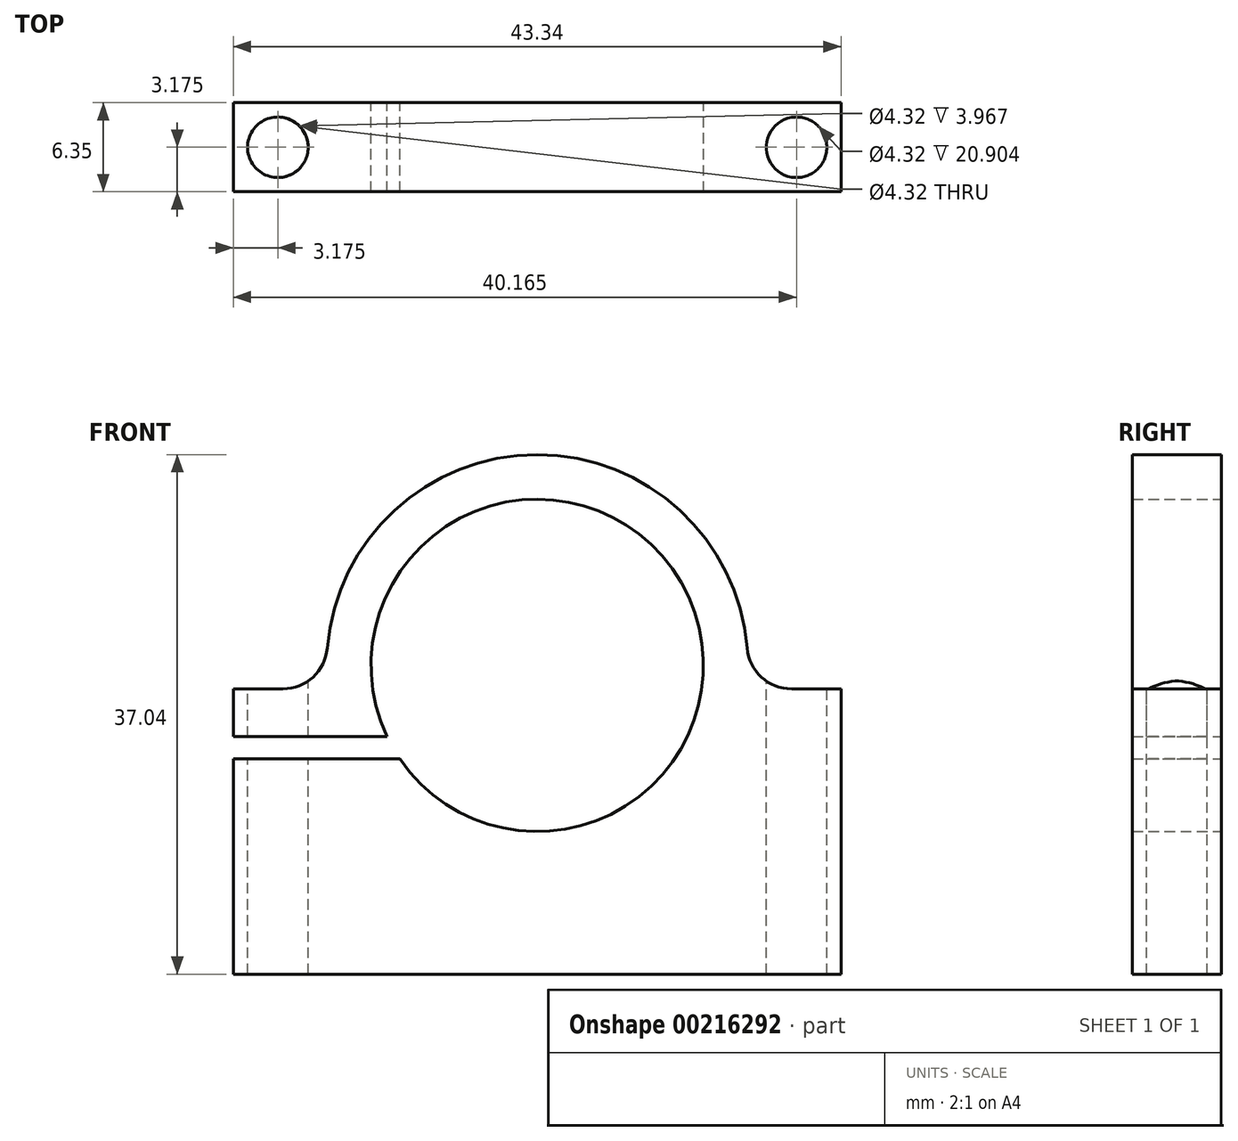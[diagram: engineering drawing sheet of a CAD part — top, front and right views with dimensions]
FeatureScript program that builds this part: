
annotation { "Feature Type Name" : "Feature", "Feature Type Description" : "" }
export const myFeature = defineFeature(function(context is Context, id is Id, definition is map)
    precondition{}
    {
        {
            var Q0;
            Q0=qCreatedBy(makeId("Front.planeOp"),FACE);
            var sketch = newSketch(context, id + "F0", { "sketchPlane" : qUnion([Q0])});
            skArc(sketch, "E0", {"start": v(-9.8, -6.67) * mm, "mid": v(10.28, 5.9) * mm, "end": v(-10.7, -5.09) * mm});
            skArc(sketch, "E1", {"start": v(14.97, 1.23) * mm, "mid": v(0, 15.02) * mm, "end": v(-14.97, 1.23) * mm});
            skLineSegment(sketch, "E2.bottom", {"start": v(-21.67, -1.68) * mm, "end": v(-18.14, -1.68) * mm});
            skLineSegment(sketch, "E2.top", {"start": v(-21.67, -22.02) * mm, "end": v(21.67, -22.02) * mm});
            skLineSegment(sketch, "E2.left", {"start": v(-21.67, -1.68) * mm, "end": v(-21.67, -5.09) * mm});
            skLineSegment(sketch, "E2.right", {"start": v(21.67, -1.68) * mm, "end": v(21.67, -22.02) * mm});
            skPoint(sketch, "E2.middle", {"position": v(0, -11.85) * mm});
            skLineSegment(sketch, "E3", {"start": v(-21.67, -5.09) * mm, "end": v(-10.7, -5.09) * mm});
            skLineSegment(sketch, "E4", {"start": v(-21.67, -6.67) * mm, "end": v(-9.8, -6.67) * mm});
            skLineSegment(sketch, "E5.trimOffspring", {"start": v(-21.67, -6.67) * mm, "end": v(-21.67, -22.02) * mm});
            skLineSegment(sketch, "E6.trimOffspring", {"start": v(18.14, -1.68) * mm, "end": v(21.67, -1.68) * mm});
            skPoint(sketch, "E7.visualSharp", {"position": v(-14.93, -1.68) * mm});
            skArc(sketch, "E7.filletArc", {"start": v(-18.14, -1.68) * mm, "mid": v(-15.99, -0.84) * mm, "end": v(-14.97, 1.23) * mm});
            skPoint(sketch, "E8.visualSharp", {"position": v(14.93, -1.68) * mm});
            skArc(sketch, "E8.filletArc", {"start": v(14.97, 1.23) * mm, "mid": v(15.99, -0.84) * mm, "end": v(18.14, -1.68) * mm});
            skSolve(sketch);
        }
        {
            var Q0;
            Q0 = qSketchRegion(id + "F0", true);
            extrude(context, id + "F1", {"entities" : qUnion([Q0]), "depth" : 6.35 * mm});
        }
        {
            var Q0;
            Q0=makeQuery(id+"F1.opExtrude","SWEPT_FACE",FACE,{"disambiguationData":[OSD([sQuery(id+"F0.wireOp",EDGE,"E2.bottom")])]});
            var sketch = newSketch(context, id + "F2", { "sketchPlane" : qUnion([Q0])});
            skLineSegment(sketch, "E9", {"start": v(-21.67, -3.18) * mm, "end": v(21.64, -3.18) * mm, "construction": true});
            skPoint(sketch, "E9.endSnap0", {"position": v(-21.67, -3.18) * mm});
            skCircle(sketch, "E10", {"center": v(-18.5, -3.18) * mm, "radius": 2.16 * mm});
            skCircle(sketch, "E11", {"center": v(18.5, -3.17) * mm, "radius": 2.16 * mm});
            skSolve(sketch);
        }
        {
            var Q0;
            Q0 = qSketchRegion(id + "F2", true);
            extrude(context, id + "F3", {"entities" : qUnion([Q0]), "operationType" : NewBodyOperationType.REMOVE, "endBound" : BoundingType.SYMMETRIC, "oppositeDirection" : true, "depth" : 76.2 * mm});
        }
    });
